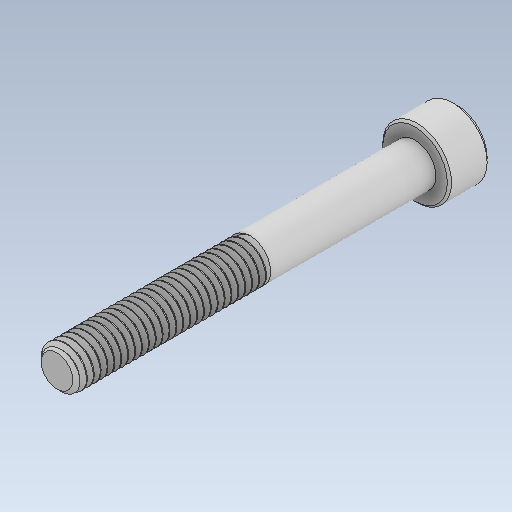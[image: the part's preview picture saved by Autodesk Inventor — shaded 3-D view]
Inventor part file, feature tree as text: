
AUTODESK INVENTOR PART (.ipt)
format: ipt  version: 2020 (Build 240168000, 168)  size: 709,632 bytes
history: native  units: in
note: dims shown in document units (in); Inventor stores cm internally (conversion verified against a paired STEP export)
features: chamfer x1
ambient origin geometry x8: Origin, YZ Plane, XZ Plane, XY Plane, X Axis, Y Axis, Z Axis, Center Point
bodies: Solid1 (feature_tree)
feature tree (1):
  chamfer  "Chamfer2"  [1 undecoded]
note: 1 required parameter value undecoded (feature->parameter linkage not recoverable at this tier; creation-order binding heuristic only, values carry confidence <= 0.55)
